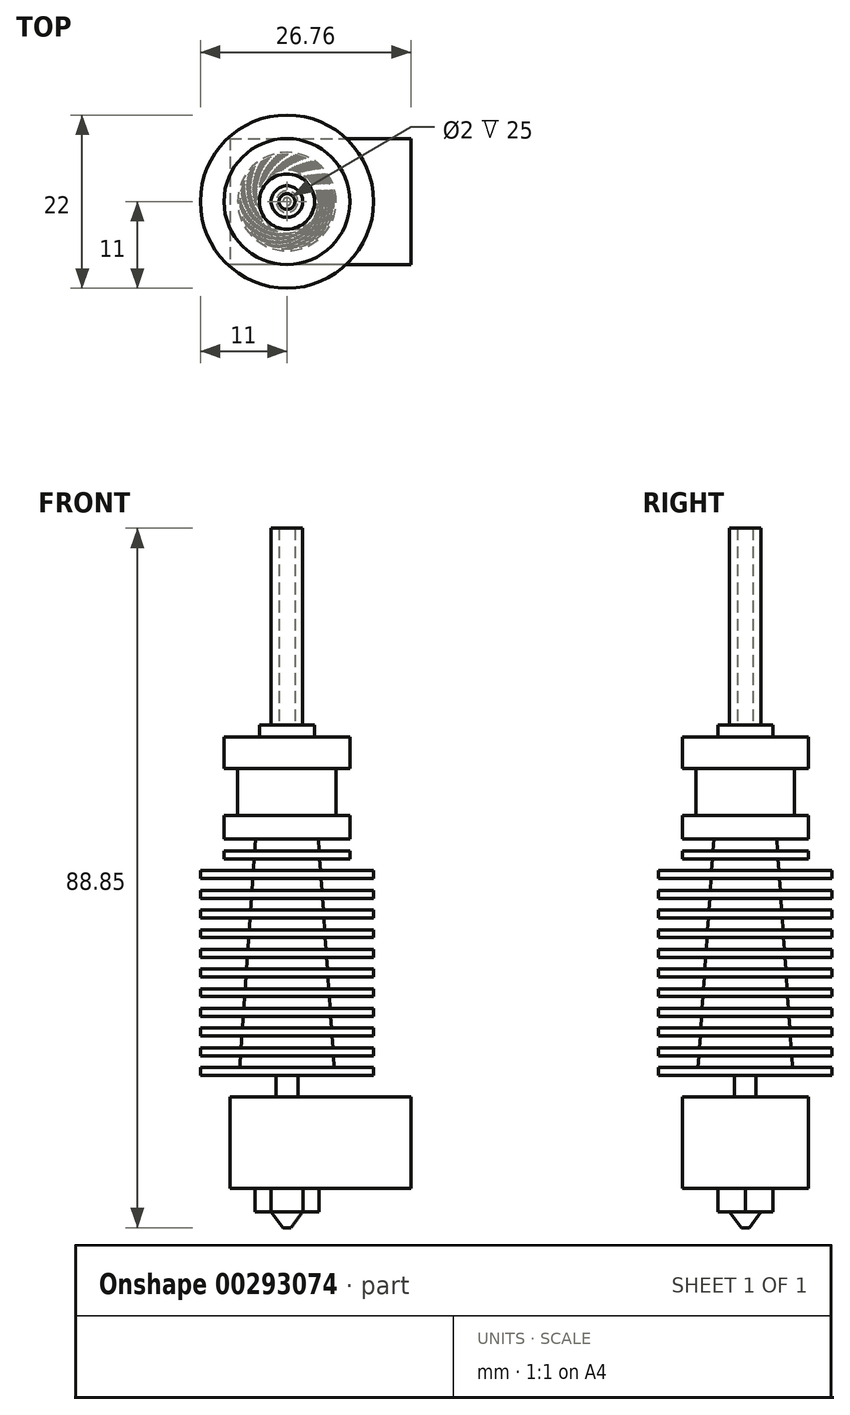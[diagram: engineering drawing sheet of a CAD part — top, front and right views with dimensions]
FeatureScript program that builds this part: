
annotation { "Feature Type Name" : "Feature", "Feature Type Description" : "" }
export const myFeature = defineFeature(function(context is Context, id is Id, definition is map)
    precondition{}
    {
        {
            var Q0;
            Q0=qCreatedBy(makeId("Right.planeOp"),FACE);
            var sketch = newSketch(context, id + "F0", { "sketchPlane" : qUnion([Q0])});
            skLineSegment(sketch, "E0", {"start": v(0, 0) * mm, "end": v(0.5, 0) * mm});
            skLineSegment(sketch, "E1", {"start": v(0, 2) * mm, "end": v(2, 2) * mm});
            skLineSegment(sketch, "E2", {"start": v(0, 2) * mm, "end": v(0, 0) * mm});
            skLineSegment(sketch, "E3", {"start": v(0.5, 0) * mm, "end": v(2, 2) * mm});
            skSolve(sketch);
        }
        {
            var Q0;
            Q0=qSketchRegion(id+"F0",true);
            var Q1;
            Q1=sQuery(id+"F0.wireOp",EDGE,"E2");
            revolve(context, id + "F1", {"entities" : qUnion([Q0]), "axis" : qUnion([Q1]), "revolveType" : RevolveType.FULL});
        }
        {
            var Q0;
            Q0=makeQuery(id+"F1.opRevolve","SWEPT_FACE",FACE,{"disambiguationData":[OSD([sQuery(id+"F0.wireOp",EDGE,"E1")])]});
            var sketch = newSketch(context, id + "F2", { "sketchPlane" : qUnion([Q0])});
            skLineSegment(sketch, "E4", {"start": v(-2.02, 3.5) * mm, "end": v(2.02, 3.5) * mm});
            skLineSegment(sketch, "E5", {"start": v(-2.02, -3.5) * mm, "end": v(2.02, -3.5) * mm});
            skLineSegment(sketch, "E6", {"start": v(-2.02, 3.5) * mm, "end": v(-4.04, 0) * mm});
            skLineSegment(sketch, "E7", {"start": v(-4.04, 0) * mm, "end": v(-2.02, -3.5) * mm});
            skLineSegment(sketch, "E8", {"start": v(2.02, -3.5) * mm, "end": v(4.04, 0) * mm});
            skLineSegment(sketch, "E9", {"start": v(4.04, 0) * mm, "end": v(2.02, 3.5) * mm});
            skLineSegment(sketch, "E10", {"start": v(4.04, 4.39) * mm, "end": v(4.04, -4.08) * mm, "construction": true});
            skLineSegment(sketch, "E11", {"start": v(-4.04, 3.84) * mm, "end": v(-4.04, -4.08) * mm, "construction": true});
            skSolve(sketch);
        }
        {
            var Q0;
            Q0=qSketchRegion(id+"F2",true);
            extrude(context, id + "F3", {"entities" : qUnion([Q0]), "operationType" : NewBodyOperationType.ADD, "depth" : 3 * mm});
        }
        {
            var Q0;
            Q0=makeQuery(id+"F3.opExtrude","CAP_FACE",FACE,{"disambiguationData":[OSD([sQuery(id+"F2.wireOp",EDGE,"E4"),sQuery(id+"F2.wireOp",EDGE,"E5"),sQuery(id+"F2.wireOp",EDGE,"E6"),sQuery(id+"F2.wireOp",EDGE,"E7"),sQuery(id+"F2.wireOp",EDGE,"E8"),sQuery(id+"F2.wireOp",EDGE,"E9")])],"isStart":false});
            var sketch = newSketch(context, id + "F4", { "sketchPlane" : qUnion([Q0])});
            skLineSegment(sketch, "E12", {"start": v(-4.04, 7.54) * mm, "end": v(-4.04, -6.8) * mm, "construction": true});
            skLineSegment(sketch, "E13", {"start": v(-7.24, 8) * mm, "end": v(-7.24, -8) * mm});
            skLineSegment(sketch, "E14", {"start": v(-7.24, 8) * mm, "end": v(15.76, 8) * mm});
            skLineSegment(sketch, "E15", {"start": v(15.76, 8) * mm, "end": v(15.76, -8) * mm});
            skLineSegment(sketch, "E16", {"start": v(15.76, -8) * mm, "end": v(-7.24, -8) * mm});
            skSolve(sketch);
        }
        {
            var Q0;
            Q0=qSketchRegion(id+"F4",true);
            extrude(context, id + "F5", {"entities" : qUnion([Q0]), "operationType" : NewBodyOperationType.ADD, "depth" : 11.6 * mm});
        }
        {
            var Q0;
            Q0=makeQuery(id+"F5.opExtrude","CAP_FACE",FACE,{"disambiguationData":[OSD([sQuery(id+"F4.wireOp",EDGE,"E13"),sQuery(id+"F4.wireOp",EDGE,"E14"),sQuery(id+"F4.wireOp",EDGE,"E15"),sQuery(id+"F4.wireOp",EDGE,"E16")])],"isStart":false});
            var sketch = newSketch(context, id + "F6", { "sketchPlane" : qUnion([Q0])});
            skCircle(sketch, "E17.0", {"center": v(0, 0) * mm, "radius": 2 * mm, "construction": true});
            skCircle(sketch, "E18", {"center": v(0, 0) * mm, "radius": 1.38 * mm});
            skSolve(sketch);
        }
        {
            var Q0;
            Q0=qSketchRegion(id+"F6",true);
            extrude(context, id + "F7", {"entities" : qUnion([Q0]), "operationType" : NewBodyOperationType.ADD, "depth" : 2.75 * mm});
        }
        {
            var Q0;
            Q0=qCreatedBy(makeId("Front.planeOp"),FACE);
            var sketch = newSketch(context, id + "F8", { "sketchPlane" : qUnion([Q0])});
            skLineSegment(sketch, "E19", {"start": v(0, 18.7) * mm, "end": v(0, 62.35) * mm});
            skLineSegment(sketch, "E20.0", {"start": v(-1.38, 19.35) * mm, "end": v(0, 19.35) * mm, "construction": true});
            skLineSegment(sketch, "E21", {"start": v(1.38, 19.35) * mm, "end": v(11, 19.35) * mm});
            skLineSegment(sketch, "E22", {"start": v(11, 19.35) * mm, "end": v(11, 20.35) * mm});
            skLineSegment(sketch, "E23", {"start": v(11, 20.35) * mm, "end": v(6, 20.35) * mm});
            skLineSegment(sketch, "E24", {"start": v(1.38, 19.35) * mm, "end": v(1.38, 20.35) * mm, "construction": true});
            skLineSegment(sketch, "E25", {"start": v(1.37, 20.35) * mm, "end": v(1.37, 21.85) * mm, "construction": true});
            skLineSegment(sketch, "E26", {"start": v(1.38, 19.35) * mm, "end": v(0, 19.35) * mm});
            skLineSegment(sketch, "E27.0.1.0", {"start": v(5.9, 21.85) * mm, "end": v(11, 21.85) * mm});
            skLineSegment(sketch, "E27.0.1.1", {"start": v(11, 21.85) * mm, "end": v(11, 22.85) * mm});
            skLineSegment(sketch, "E27.0.1.2", {"start": v(11, 22.85) * mm, "end": v(5.83, 22.85) * mm});
            skLineSegment(sketch, "E27.0.2.0", {"start": v(5.72, 24.35) * mm, "end": v(11, 24.35) * mm});
            skLineSegment(sketch, "E27.0.2.1", {"start": v(11, 24.35) * mm, "end": v(11, 25.35) * mm});
            skLineSegment(sketch, "E27.0.2.2", {"start": v(11, 25.35) * mm, "end": v(5.65, 25.35) * mm});
            skLineSegment(sketch, "E27.0.3.0", {"start": v(5.55, 26.85) * mm, "end": v(11, 26.85) * mm});
            skLineSegment(sketch, "E27.0.3.1", {"start": v(11, 26.85) * mm, "end": v(11, 27.85) * mm});
            skLineSegment(sketch, "E27.0.3.2", {"start": v(11, 27.85) * mm, "end": v(5.48, 27.85) * mm});
            skLineSegment(sketch, "E27.0.4.0", {"start": v(5.38, 29.35) * mm, "end": v(11, 29.35) * mm});
            skLineSegment(sketch, "E27.0.4.1", {"start": v(11, 29.35) * mm, "end": v(11, 30.35) * mm});
            skLineSegment(sketch, "E27.0.4.2", {"start": v(11, 30.35) * mm, "end": v(5.3, 30.35) * mm});
            skLineSegment(sketch, "E27.0.5.0", {"start": v(5.2, 31.85) * mm, "end": v(11, 31.85) * mm});
            skLineSegment(sketch, "E27.0.5.1", {"start": v(11, 31.85) * mm, "end": v(11, 32.85) * mm});
            skLineSegment(sketch, "E27.0.5.2", {"start": v(11, 32.85) * mm, "end": v(5.14, 32.85) * mm});
            skLineSegment(sketch, "E27.0.6.0", {"start": v(5.03, 34.35) * mm, "end": v(11, 34.35) * mm});
            skLineSegment(sketch, "E27.0.6.1", {"start": v(11, 34.35) * mm, "end": v(11, 35.35) * mm});
            skLineSegment(sketch, "E27.0.6.2", {"start": v(11, 35.35) * mm, "end": v(4.96, 35.35) * mm});
            skLineSegment(sketch, "E27.0.7.0", {"start": v(4.86, 36.85) * mm, "end": v(11, 36.85) * mm});
            skLineSegment(sketch, "E27.0.7.1", {"start": v(11, 36.85) * mm, "end": v(11, 37.85) * mm});
            skLineSegment(sketch, "E27.0.7.2", {"start": v(11, 37.85) * mm, "end": v(4.79, 37.85) * mm});
            skLineSegment(sketch, "E27.0.8.0", {"start": v(4.69, 39.35) * mm, "end": v(11, 39.35) * mm});
            skLineSegment(sketch, "E27.0.8.1", {"start": v(11, 39.35) * mm, "end": v(11, 40.35) * mm});
            skLineSegment(sketch, "E27.0.8.2", {"start": v(11, 40.35) * mm, "end": v(4.62, 40.35) * mm});
            skLineSegment(sketch, "E27.0.9.0", {"start": v(4.51, 41.85) * mm, "end": v(11, 41.85) * mm});
            skLineSegment(sketch, "E27.0.9.1", {"start": v(11, 41.85) * mm, "end": v(11, 42.85) * mm});
            skLineSegment(sketch, "E27.0.9.2", {"start": v(11, 42.85) * mm, "end": v(4.44, 42.85) * mm});
            skLineSegment(sketch, "E27.direction1", {"start": v(1.37, 19.35) * mm, "end": v(26.38, 19.35) * mm, "construction": true});
            skLineSegment(sketch, "E28", {"start": v(4.34, 44.35) * mm, "end": v(11, 44.35) * mm});
            skLineSegment(sketch, "E29", {"start": v(11, 44.35) * mm, "end": v(11, 45.35) * mm});
            skLineSegment(sketch, "E30", {"start": v(11, 45.35) * mm, "end": v(4.27, 45.35) * mm});
            skLineSegment(sketch, "E31", {"start": v(6, 20.35) * mm, "end": v(5.9, 21.85) * mm});
            skPoint(sketch, "E32.orphan", {"position": v(1.38, 21.85) * mm});
            skPoint(sketch, "E33.orphan", {"position": v(1.38, 24.35) * mm});
            skLineSegment(sketch, "E34.trimOffspring", {"start": v(5.83, 22.85) * mm, "end": v(5.72, 24.35) * mm});
            skLineSegment(sketch, "E35.trimOffspring", {"start": v(5.65, 25.35) * mm, "end": v(5.55, 26.85) * mm});
            skPoint(sketch, "E36.orphan", {"position": v(1.38, 26.85) * mm});
            skLineSegment(sketch, "E37.trimOffspring", {"start": v(5.48, 27.85) * mm, "end": v(5.38, 29.35) * mm});
            skPoint(sketch, "E38.orphan", {"position": v(1.38, 29.35) * mm});
            skPoint(sketch, "E39.orphan", {"position": v(1.38, 31.85) * mm});
            skPoint(sketch, "E40.orphan", {"position": v(1.38, 34.35) * mm});
            skPoint(sketch, "E41.orphan", {"position": v(1.38, 36.85) * mm});
            skPoint(sketch, "E42.orphan", {"position": v(1.38, 39.35) * mm});
            skPoint(sketch, "E43.orphan", {"position": v(1.38, 41.85) * mm});
            skLineSegment(sketch, "E44.trimOffspring", {"start": v(4.44, 42.85) * mm, "end": v(4.34, 44.35) * mm});
            skLineSegment(sketch, "E45.trimOffspring", {"start": v(4.62, 40.35) * mm, "end": v(4.51, 41.85) * mm});
            skLineSegment(sketch, "E46.trimOffspring", {"start": v(4.79, 37.85) * mm, "end": v(4.69, 39.35) * mm});
            skLineSegment(sketch, "E47.trimOffspring", {"start": v(4.96, 35.35) * mm, "end": v(4.86, 36.85) * mm});
            skLineSegment(sketch, "E48.trimOffspring", {"start": v(5.14, 32.85) * mm, "end": v(5.03, 34.35) * mm});
            skLineSegment(sketch, "E49.trimOffspring", {"start": v(5.3, 30.35) * mm, "end": v(5.2, 31.85) * mm});
            skLineSegment(sketch, "E50", {"start": v(4.27, 45.35) * mm, "end": v(4.17, 46.85) * mm});
            skLineSegment(sketch, "E51", {"start": v(0, 45.35) * mm, "end": v(0, 46.85) * mm});
            skLineSegment(sketch, "E52", {"start": v(4.17, 46.85) * mm, "end": v(8, 46.85) * mm});
            skLineSegment(sketch, "E53", {"start": v(8, 46.85) * mm, "end": v(8, 47.85) * mm});
            skLineSegment(sketch, "E54", {"start": v(8, 47.85) * mm, "end": v(4.1, 47.85) * mm});
            skLineSegment(sketch, "E55", {"start": v(4, 49.35) * mm, "end": v(8, 49.35) * mm});
            skLineSegment(sketch, "E56", {"start": v(8, 49.35) * mm, "end": v(8, 52.35) * mm});
            skLineSegment(sketch, "E57", {"start": v(8, 52.35) * mm, "end": v(6.25, 52.35) * mm});
            skLineSegment(sketch, "E58.trimOffspring", {"start": v(4.1, 47.85) * mm, "end": v(4, 49.35) * mm});
            skLineSegment(sketch, "E59", {"start": v(6.25, 52.35) * mm, "end": v(6.25, 58.35) * mm});
            skLineSegment(sketch, "E60", {"start": v(6.25, 58.35) * mm, "end": v(8, 58.35) * mm});
            skLineSegment(sketch, "E61", {"start": v(8, 58.35) * mm, "end": v(8, 62.35) * mm});
            skLineSegment(sketch, "E62", {"start": v(8, 62.35) * mm, "end": v(0, 62.35) * mm});
            skSolve(sketch);
        }
        {
            var Q0;
            Q0=qSketchRegion(id+"F8",true);
            var Q1;
            Q1=sQuery(id+"F8.wireOp",EDGE,"E19");
            revolve(context, id + "F9", {"operationType" : NewBodyOperationType.ADD, "entities" : qUnion([Q0]), "axis" : qUnion([Q1]), "revolveType" : RevolveType.FULL});
        }
        {
            var Q0;
            Q0=makeQuery(id+"F9.opRevolve","SWEPT_FACE",FACE,{"disambiguationData":[OSD([sQuery(id+"F8.wireOp",EDGE,"E62")])]});
            var sketch = newSketch(context, id + "F10", { "sketchPlane" : qUnion([Q0])});
            skCircle(sketch, "E63.0", {"center": v(0, 0) * mm, "radius": 8 * mm, "construction": true});
            skCircle(sketch, "E64", {"center": v(0, 0) * mm, "radius": 3.5 * mm});
            skSolve(sketch);
        }
        {
            var Q0;
            Q0=qSketchRegion(id+"F10",true);
            extrude(context, id + "F11", {"entities" : qUnion([Q0]), "operationType" : NewBodyOperationType.ADD, "depth" : 1.5 * mm});
        }
        {
            var Q0;
            Q0=makeQuery(id+"F11.opExtrude","CAP_FACE",FACE,{"disambiguationData":[OSD([sQuery(id+"F10.wireOp",EDGE,"E64")])],"isStart":false});
            var sketch = newSketch(context, id + "F12", { "sketchPlane" : qUnion([Q0])});
            skCircle(sketch, "E65.0", {"center": v(0, 0) * mm, "radius": 3.5 * mm, "construction": true});
            skCircle(sketch, "E66", {"center": v(0, 0) * mm, "radius": 2 * mm});
            skCircle(sketch, "E67", {"center": v(0, 0) * mm, "radius": 1 * mm});
            skSolve(sketch);
        }
        {
            var Q0;
            Q0=qSketchRegion(id+"F12",true);
            extrude(context, id + "F13", {"entities" : qUnion([Q0]), "operationType" : NewBodyOperationType.ADD, "depth" : 25 * mm});
        }
    });
